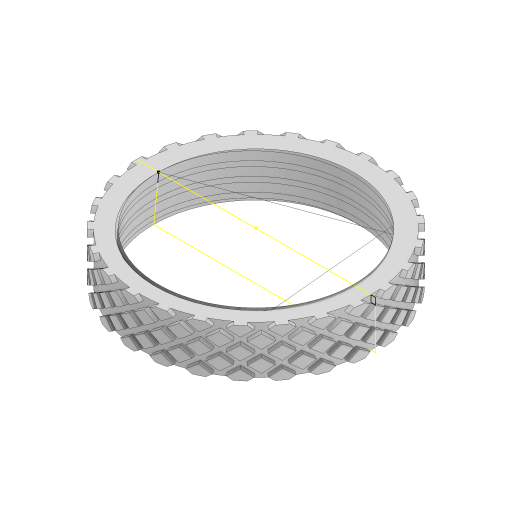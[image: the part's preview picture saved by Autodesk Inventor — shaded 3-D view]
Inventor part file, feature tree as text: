
AUTODESK INVENTOR PART (.ipt)
format: ipt  version: 2023 (Build 270158000, 158)  size: 1,654,784 bytes
history: native  units: mm
features: helix x6, sketch x4, pattern_circular x2, extrude x1, draft x1
ambient origin geometry x8: Origin, YZ Plane, XZ Plane, XY Plane, X Axis, Y Axis, Z Axis, Center Point
bodies: Solid1 (feature_tree)
feature tree (14):
  extrude  "Extrusion1"  Depth=6.52mm TaperAngle=0.0deg
  draft  "FaceDraft1"
  sketch  "Sketch2"  dims[d7=2.0mm d8=9.0mm d9=10.0mm d10=1.047198mm d11=90.0deg d12=90.0deg d13=0.0mm d14=0.0mm d15=2.0mm d16=3.0mm d17=10.0mm d18=-1.047198mm d19=90.0deg d20=90.0deg d21=0.0mm d22=0.0mm d23=3.0mm]
  sketch  "Sketch4"  dims[d52=70.0mm d53=9.0mm d54=10.0mm d55=0.0mm d56=90.0deg d57=90.0deg d58=0.0mm d59=0.0mm d60=70.0mm d61=9.0mm d62=10.0mm d63=0.0mm d64=90.0deg d65=90.0deg d66=0.0mm d67=0.0mm d68=250.0mm d69=360.0deg]
  helix  "Coil1"  [1 undecoded]
  helix  "Coil2"  [1 undecoded]
  sketch  "Sketch7"  dims[d71=70.0mm d72=9.0mm d73=10.0mm d74=0.0mm d75=90.0deg d76=90.0deg d77=0.0mm d78=0.0mm d79=70.0mm d80=9.0mm d81=10.0mm d82=0.0mm d83=90.0deg d84=90.0deg d85=0.0mm d86=0.0mm d87=250.0mm d88=360.0deg]
  helix  "Coil6"  [1 undecoded]
  helix  "Coil7"  [1 undecoded]
  pattern_circular  "Circular Pattern1"  [2 undecoded]
  helix  "Coil8"  [1 undecoded]
  helix  "Coil9"  [1 undecoded]
  pattern_circular  "Circular Pattern2"  [2 undecoded]
  sketch  "Sketch1"  dims[d0=26.5mm d2=6.52mm d3=0.0mm d4=1.047198mm]
note: 10 required parameter values undecoded (feature->parameter linkage not recoverable at this tier; creation-order binding heuristic only, values carry confidence <= 0.55)
